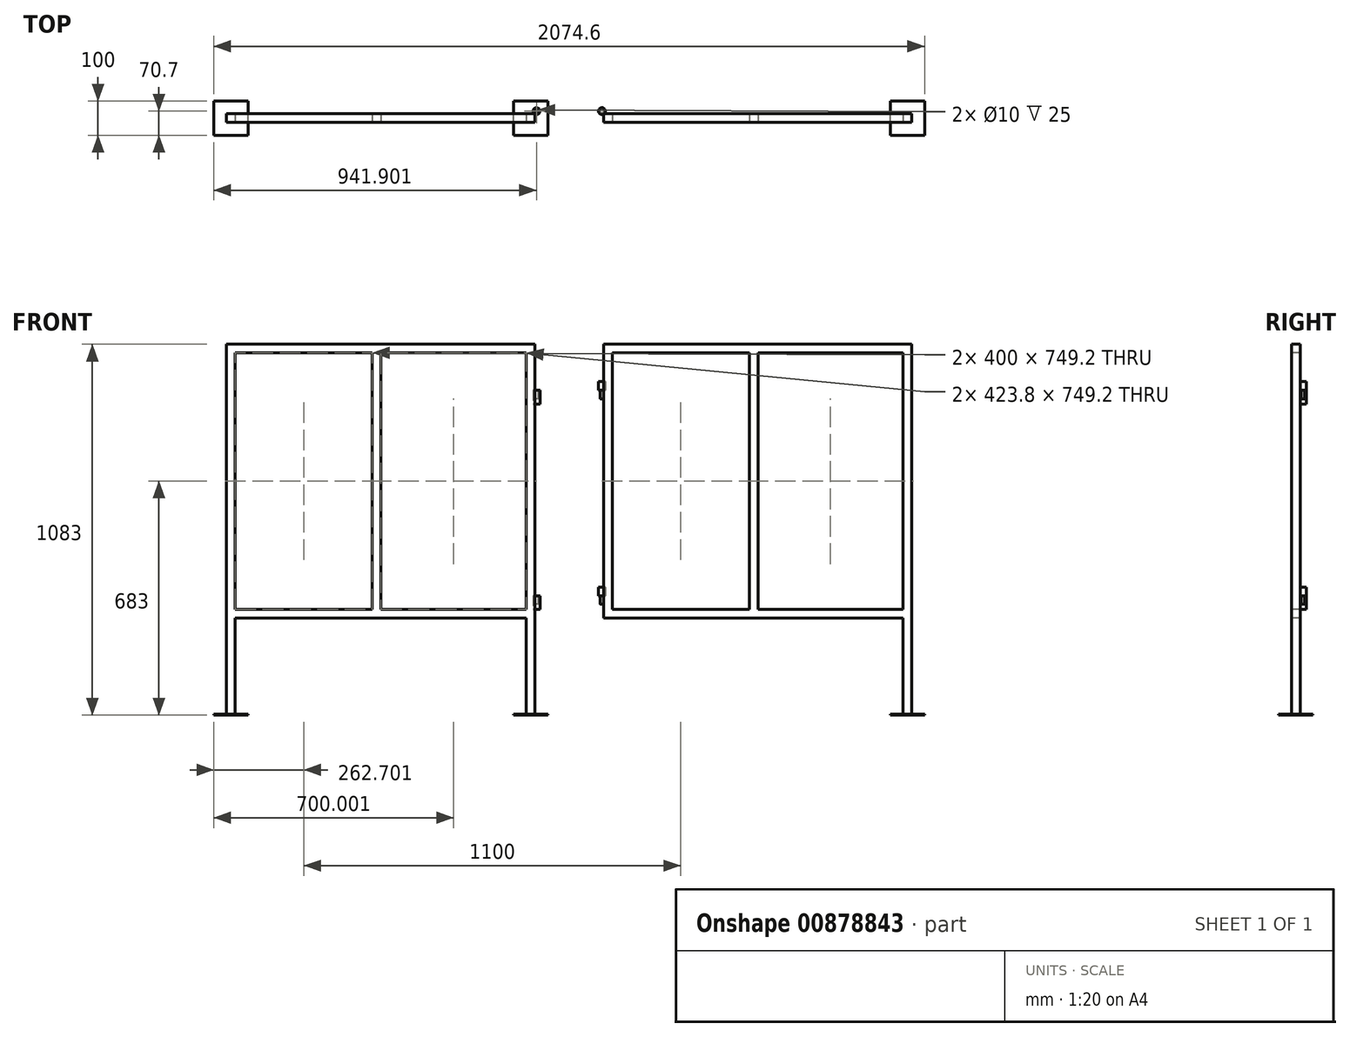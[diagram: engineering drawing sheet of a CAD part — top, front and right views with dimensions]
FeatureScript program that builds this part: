
annotation { "Feature Type Name" : "Feature", "Feature Type Description" : "" }
export const myFeature = defineFeature(function(context is Context, id is Id, definition is map)
    precondition{}
    {
        {
            var Q0;
            Q0=qCreatedBy(makeId("Front.planeOp"),FACE);
            var sketch = newSketch(context, id + "F0", { "sketchPlane" : qUnion([Q0])});
            skLineSegment(sketch, "E0.bottom", {"start": v(-413.52, 774.6) * mm, "end": v(486.48, 774.6) * mm});
            skLineSegment(sketch, "E0.top", {"start": v(-413.52, -305.4) * mm, "end": v(-388.12, -305.4) * mm});
            skLineSegment(sketch, "E0.left", {"start": v(-413.52, 774.6) * mm, "end": v(-413.52, -305.4) * mm});
            skLineSegment(sketch, "E0.right", {"start": v(486.48, 774.6) * mm, "end": v(486.48, -305.4) * mm});
            skLineSegment(sketch, "E1.top", {"start": v(-388.12, -25.4) * mm, "end": v(461.08, -25.4) * mm});
            skLineSegment(sketch, "E1.left", {"start": v(-388.12, -305.4) * mm, "end": v(-388.12, -25.4) * mm});
            skLineSegment(sketch, "E1.right", {"start": v(461.08, -305.4) * mm, "end": v(461.08, -25.4) * mm});
            skLineSegment(sketch, "E2.bottom", {"start": v(-388.12, 749.2) * mm, "end": v(11.88, 749.2) * mm});
            skLineSegment(sketch, "E2.top", {"start": v(-388.12, 0) * mm, "end": v(11.88, 0) * mm});
            skLineSegment(sketch, "E2.left", {"start": v(-388.12, 749.2) * mm, "end": v(-388.12, 0) * mm});
            skLineSegment(sketch, "E2.right", {"start": v(11.88, 749.2) * mm, "end": v(11.88, 0) * mm});
            skLineSegment(sketch, "E3.bottom", {"start": v(37.28, 749.2) * mm, "end": v(461.08, 749.2) * mm});
            skLineSegment(sketch, "E3.top", {"start": v(37.28, 0) * mm, "end": v(461.08, 0) * mm});
            skLineSegment(sketch, "E3.left", {"start": v(37.28, 749.2) * mm, "end": v(37.28, 0) * mm});
            skLineSegment(sketch, "E3.right", {"start": v(461.08, 749.2) * mm, "end": v(461.08, 0) * mm});
            skLineSegment(sketch, "E4.trimOffspring", {"start": v(461.08, -305.4) * mm, "end": v(486.48, -305.4) * mm});
            skLineSegment(sketch, "E5.1.0.0", {"start": v(1137.28, 749.2) * mm, "end": v(1137.28, 0) * mm});
            skLineSegment(sketch, "E5.1.0.1", {"start": v(1137.28, 749.2) * mm, "end": v(1561.08, 749.2) * mm});
            skLineSegment(sketch, "E5.1.0.2", {"start": v(711.88, 0) * mm, "end": v(1111.88, 0) * mm});
            skLineSegment(sketch, "E5.1.0.3", {"start": v(711.88, 749.2) * mm, "end": v(1111.88, 749.2) * mm});
            skLineSegment(sketch, "E5.1.0.4", {"start": v(1111.88, 749.2) * mm, "end": v(1111.88, 0) * mm});
            skLineSegment(sketch, "E5.1.0.5", {"start": v(686.48, 774.6) * mm, "end": v(1586.48, 774.6) * mm});
            skLineSegment(sketch, "E5.1.0.6", {"start": v(1561.08, -305.4) * mm, "end": v(1561.08, -25.4) * mm});
            skLineSegment(sketch, "E5.1.0.7", {"start": v(1561.08, 749.2) * mm, "end": v(1561.08, 0) * mm});
            skLineSegment(sketch, "E5.1.0.8", {"start": v(686.48, 774.6) * mm, "end": v(686.48, -25.4) * mm});
            skLineSegment(sketch, "E5.1.0.9", {"start": v(711.88, 749.2) * mm, "end": v(711.88, 0) * mm});
            skLineSegment(sketch, "E5.1.0.10", {"start": v(711.88, -25.4) * mm, "end": v(1561.08, -25.4) * mm});
            skLineSegment(sketch, "E5.1.0.11", {"start": v(1137.28, 0) * mm, "end": v(1561.08, 0) * mm});
            skLineSegment(sketch, "E5.1.0.13", {"start": v(1586.48, 774.6) * mm, "end": v(1586.48, -305.4) * mm});
            skLineSegment(sketch, "E5.1.0.14", {"start": v(686.48, -305.4) * mm, "end": v(711.88, -305.4) * mm});
            skLineSegment(sketch, "E5.1.0.15", {"start": v(1561.08, -305.4) * mm, "end": v(1586.48, -305.4) * mm});
            skLineSegment(sketch, "E5.direction1", {"start": v(-413.52, -305.4) * mm, "end": v(686.48, -305.4) * mm, "construction": true});
            skLineSegment(sketch, "E6", {"start": v(711.88, -25.4) * mm, "end": v(686.48, -25.4) * mm});
            skSolve(sketch);
        }
        {
            var Q0;
            Q0=makeQuery(id+"F0.imprint","IMPRINT",FACE,{"disambiguationData":[TD([[makeQuery(id+"F0.imprint","IMPRINT",EDGE,{"derivedFrom":sQuery(id+"F0.wireOp",EDGE,"E0.bottom")}),-1.0]])]});
            var Q1;
            Q1=makeQuery(id+"F0.imprint","IMPRINT",FACE,{"disambiguationData":[TD([[makeQuery(id+"F0.imprint","IMPRINT",EDGE,{"derivedFrom":sQuery(id+"F0.wireOp",EDGE,"E5.1.0.0")}),-1.0]])]});
            extrude(context, id + "F1", {"entities" : qUnion([Q0, Q1]), "oppositeDirection" : true, "depth" : 25.4 * mm, "offsetDistance" : 25 * mm});
        }
        {
            var Q0;
            {var subQ0=sQuery(id+"F0.wireOp",EDGE,"E0.top");Q0=makeQuery(id+"F1.opExtrude","SWEPT_FACE",FACE,{"disambiguationData":[OSD([subQ0]),TDD([makeQuery(id+"F0.imprint","IMPRINT",EDGE,{"disambiguationData":[TD([[makeQuery(id+"F0.imprint","INTERSECT",VERTEX,{"derivedFrom":[subQ0,sQuery(id+"F0.wireOp",EDGE,"E0.left")]}),-1.0]])],"derivedFrom":subQ0})])]});}
            var sketch = newSketch(context, id + "F2", { "sketchPlane" : qUnion([Q0])});
            skLineSegment(sketch, "E7.bottom", {"start": v(-450.82, 37.3) * mm, "end": v(-350.82, 37.3) * mm});
            skLineSegment(sketch, "E7.top", {"start": v(-450.82, -62.7) * mm, "end": v(-350.82, -62.7) * mm});
            skLineSegment(sketch, "E7.left", {"start": v(-450.82, 37.3) * mm, "end": v(-450.82, -62.7) * mm});
            skLineSegment(sketch, "E7.right", {"start": v(-350.82, 37.3) * mm, "end": v(-350.82, -62.7) * mm});
            skLineSegment(sketch, "E8.bottom", {"start": v(423.78, 37.3) * mm, "end": v(523.78, 37.3) * mm});
            skLineSegment(sketch, "E8.top", {"start": v(423.78, -62.7) * mm, "end": v(523.78, -62.7) * mm});
            skLineSegment(sketch, "E8.left", {"start": v(423.78, 37.3) * mm, "end": v(423.78, -62.7) * mm});
            skLineSegment(sketch, "E8.right", {"start": v(523.78, 37.3) * mm, "end": v(523.78, -62.7) * mm});
            skSolve(sketch);
        }
        {
            var Q0;
            Q0 = qSketchRegion(id + "F2", true);
            extrude(context, id + "F3", {"entities" : qUnion([Q0]), "operationType" : NewBodyOperationType.ADD, "depth" : 3 * mm, "offsetDistance" : 25 * mm});
        }
        {
            var Q0;
            Q0=makeQuery(id+"F1.opExtrude","SWEPT_FACE",FACE,{"disambiguationData":[OSD([sQuery(id+"F0.wireOp",EDGE,"E5.1.0.15")])]});
            var sketch = newSketch(context, id + "F4", { "sketchPlane" : qUnion([Q0])});
            skLineSegment(sketch, "E9.bottom", {"start": v(1523.78, 37.3) * mm, "end": v(1623.78, 37.3) * mm});
            skLineSegment(sketch, "E9.top", {"start": v(1523.78, -62.7) * mm, "end": v(1623.78, -62.7) * mm});
            skLineSegment(sketch, "E9.left", {"start": v(1523.78, 37.3) * mm, "end": v(1523.78, -62.7) * mm});
            skLineSegment(sketch, "E9.right", {"start": v(1623.78, 37.3) * mm, "end": v(1623.78, -62.7) * mm});
            skSolve(sketch);
        }
        {
            var Q0;
            Q0 = qSketchRegion(id + "F4", true);
            extrude(context, id + "F5", {"entities" : qUnion([Q0]), "operationType" : NewBodyOperationType.ADD, "depth" : 3 * mm, "offsetDistance" : 25 * mm});
        }
        {
            var Q0;
            Q0=makeQuery(id+"F1.opExtrude","SWEPT_FACE",FACE,{"disambiguationData":[OSD([sQuery(id+"F0.wireOp",EDGE,"E3.top")])]});
            var sketch = newSketch(context, id + "F6", { "sketchPlane" : qUnion([Q0])});
            skCircle(sketch, "E10", {"center": v(491.08, 33.4) * mm, "radius": 10 * mm});
            skSolve(sketch);
        }
        {
            var Q0;
            Q0 = qSketchRegion(id + "F6", true);
            extrude(context, id + "F7", {"entities" : qUnion([Q0]), "operationType" : NewBodyOperationType.ADD, "depth" : 40 * mm, "offsetDistance" : 25 * mm});
        }
        {
            var Q0;
            Q0=makeQuery(id+"F7.opExtrude","CAP_FACE",FACE,{"disambiguationData":[OSD([sQuery(id+"F6.wireOp",EDGE,"E10")])],"isStart":false});
            var sketch = newSketch(context, id + "F8", { "sketchPlane" : qUnion([Q0])});
            skCircle(sketch, "E11", {"center": v(491.08, 33.4) * mm, "radius": 5 * mm});
            skSolve(sketch);
        }
        {
            var Q0;
            Q0 = qSketchRegion(id + "F8", true);
            extrude(context, id + "F9", {"entities" : qUnion([Q0]), "operationType" : NewBodyOperationType.REMOVE, "oppositeDirection" : true, "depth" : 25 * mm, "offsetDistance" : 25 * mm});
        }
        {
            var Q0;
            Q0=makeQuery(id+"F1.opExtrude","SWEPT_FACE",FACE,{"disambiguationData":[OSD([sQuery(id+"F0.wireOp",EDGE,"E3.top")])]});
            cPlane(context, id + "F10", {"entities" : qUnion([Q0]), "cplaneType" : CPlaneType.OFFSET, "offset" : 600 * mm, "width" : 150 * mm, "height" : 150 * mm});
        }
        {
            var Q0;
            Q0=qCreatedBy(id+"F10.planeOp",FACE);
            var sketch = newSketch(context, id + "F11", { "sketchPlane" : qUnion([Q0])});
            skCircle(sketch, "E12", {"center": v(491.08, 33.4) * mm, "radius": 10 * mm});
            skSolve(sketch);
        }
        {
            var Q0;
            Q0 = qSketchRegion(id + "F11", true);
            extrude(context, id + "F12", {"entities" : qUnion([Q0]), "operationType" : NewBodyOperationType.ADD, "depth" : 40 * mm, "offsetDistance" : 25 * mm});
        }
        {
            var Q0;
            Q0=makeQuery(id+"F12.opExtrude","CAP_FACE",FACE,{"disambiguationData":[OSD([sQuery(id+"F11.wireOp",EDGE,"E12")])],"isStart":false});
            var sketch = newSketch(context, id + "F13", { "sketchPlane" : qUnion([Q0])});
            skCircle(sketch, "E13", {"center": v(491.08, 33.4) * mm, "radius": 5 * mm});
            skSolve(sketch);
        }
        {
            var Q0;
            Q0 = qSketchRegion(id + "F13", true);
            extrude(context, id + "F14", {"entities" : qUnion([Q0]), "operationType" : NewBodyOperationType.REMOVE, "oppositeDirection" : true, "depth" : 25 * mm, "offsetDistance" : 25 * mm});
        }
        {
            var Q0;
            Q0=makeQuery(id+"F12.opExtrude","CAP_FACE",FACE,{"disambiguationData":[OSD([sQuery(id+"F11.wireOp",EDGE,"E12")])],"isStart":false});
            cPlane(context, id + "F15", {"entities" : qUnion([Q0]), "cplaneType" : CPlaneType.OFFSET, "offset" : 0 * mm, "width" : 150 * mm, "height" : 150 * mm});
        }
        {
            var Q0;
            Q0=makeQuery(id+"F7.opExtrude","CAP_FACE",FACE,{"disambiguationData":[OSD([sQuery(id+"F6.wireOp",EDGE,"E10")])],"isStart":false});
            cPlane(context, id + "F16", {"entities" : qUnion([Q0]), "cplaneType" : CPlaneType.OFFSET, "offset" : 0 * mm, "width" : 150 * mm, "height" : 150 * mm});
        }
        {
            var Q0;
            Q0=qCreatedBy(id+"F16.planeOp",FACE);
            var sketch = newSketch(context, id + "F17", { "sketchPlane" : qUnion([Q0])});
            skCircle(sketch, "E14", {"center": v(681.88, 33.4) * mm, "radius": 10 * mm});
            skSolve(sketch);
        }
        {
            var Q0;
            Q0 = qSketchRegion(id + "F17", true);
            extrude(context, id + "F18", {"entities" : qUnion([Q0]), "operationType" : NewBodyOperationType.ADD, "depth" : 25 * mm, "offsetDistance" : 25 * mm});
        }
        {
            var Q0;
            Q0=makeQuery(id+"F18.opExtrude","CAP_FACE",FACE,{"disambiguationData":[OSD([sQuery(id+"F17.wireOp",EDGE,"E14")])],"isStart":true});
            var sketch = newSketch(context, id + "F19", { "sketchPlane" : qUnion([Q0])});
            skCircle(sketch, "E15", {"center": v(681.88, -33.4) * mm, "radius": 5 * mm});
            skSolve(sketch);
        }
        {
            var Q0;
            Q0 = qSketchRegion(id + "F19", true);
            extrude(context, id + "F20", {"entities" : qUnion([Q0]), "operationType" : NewBodyOperationType.ADD, "depth" : 25 * mm, "offsetDistance" : 25 * mm});
        }
        {
            var Q0;
            Q0=qCreatedBy(id+"F15.planeOp",FACE);
            var sketch = newSketch(context, id + "F21", { "sketchPlane" : qUnion([Q0])});
            skCircle(sketch, "E16", {"center": v(681.88, 33.4) * mm, "radius": 10 * mm});
            skSolve(sketch);
        }
        {
            var Q0;
            Q0 = qSketchRegion(id + "F21", true);
            extrude(context, id + "F22", {"entities" : qUnion([Q0]), "operationType" : NewBodyOperationType.ADD, "depth" : 25 * mm, "offsetDistance" : 25 * mm});
        }
        {
            var Q0;
            Q0=makeQuery(id+"F22.opExtrude","CAP_FACE",FACE,{"disambiguationData":[OSD([sQuery(id+"F21.wireOp",EDGE,"E16")])],"isStart":true});
            var sketch = newSketch(context, id + "F23", { "sketchPlane" : qUnion([Q0])});
            skCircle(sketch, "E17", {"center": v(681.88, -33.4) * mm, "radius": 5 * mm});
            skSolve(sketch);
        }
        {
            var Q0;
            Q0 = qSketchRegion(id + "F23", true);
            extrude(context, id + "F24", {"entities" : qUnion([Q0]), "operationType" : NewBodyOperationType.ADD, "depth" : 25 * mm, "offsetDistance" : 25 * mm});
        }
    });
